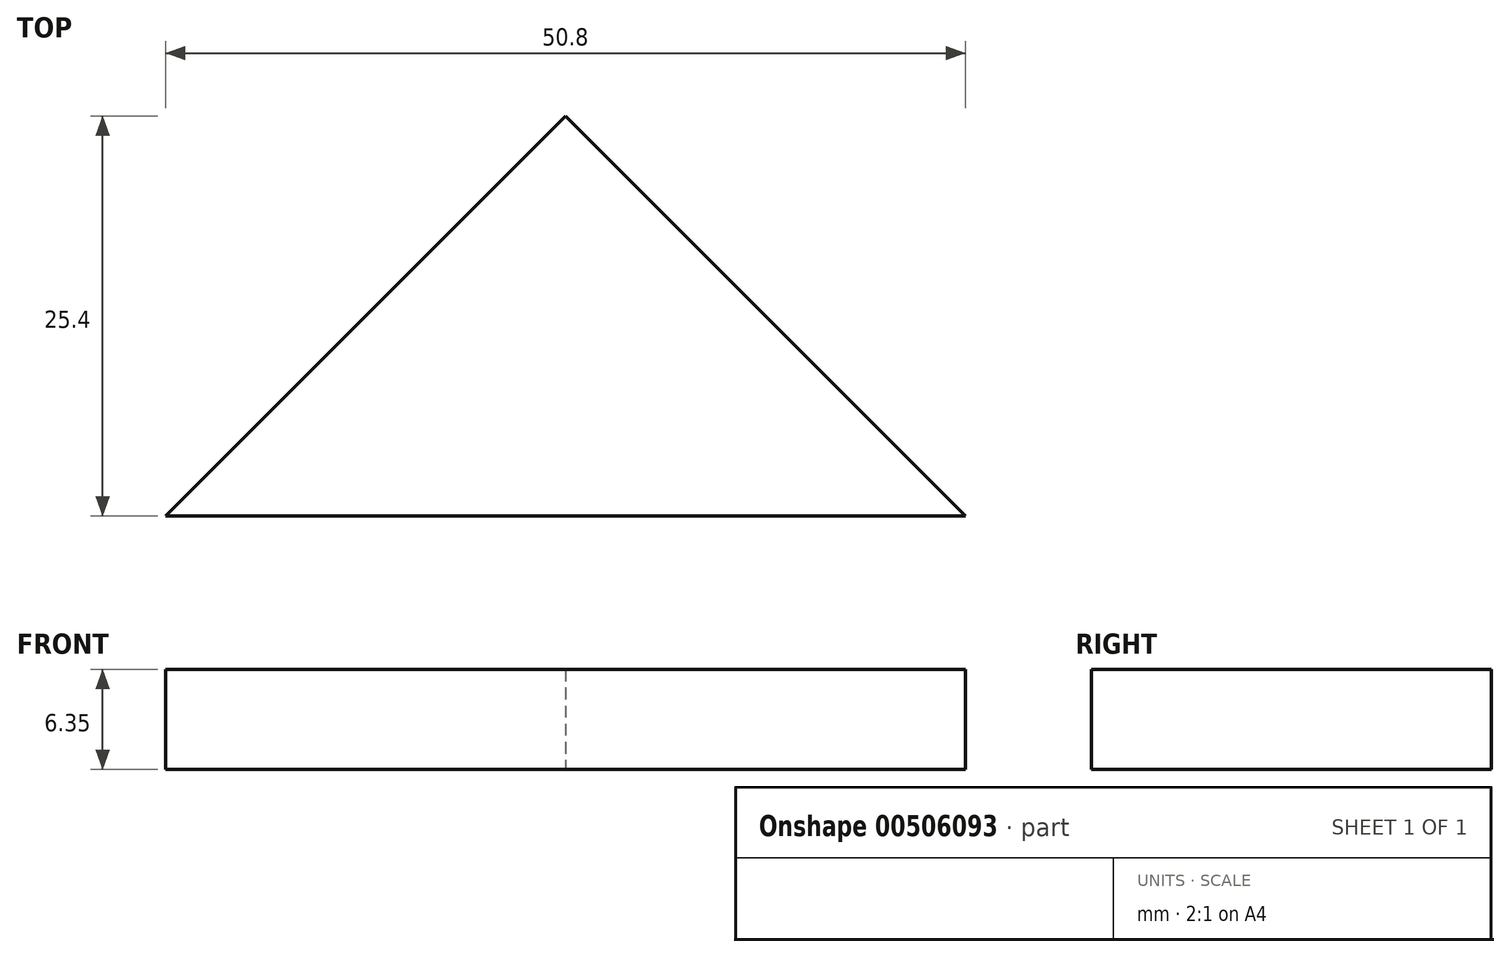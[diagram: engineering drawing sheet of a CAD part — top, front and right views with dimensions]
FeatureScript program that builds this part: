
annotation { "Feature Type Name" : "Feature", "Feature Type Description" : "" }
export const myFeature = defineFeature(function(context is Context, id is Id, definition is map)
    precondition{}
    {
        {
            var Q0;
            Q0=qCreatedBy(makeId("Top.planeOp"),FACE);
            var sketch = newSketch(context, id + "F0", { "sketchPlane" : qUnion([Q0])});
            skLineSegment(sketch, "E0.bottom", {"start": v(0, 0) * mm, "end": v(50.8, 0) * mm});
            skLineSegment(sketch, "E1", {"start": v(25.4, 25.4) * mm, "end": v(50.8, 0) * mm});
            skLineSegment(sketch, "E2", {"start": v(0, 0) * mm, "end": v(25.4, 25.4) * mm});
            skSolve(sketch);
        }
        {
            var Q0;
            Q0=makeQuery(id+"F0.imprint","IMPRINT",FACE,{"disambiguationData":[TD([[makeQuery(id+"F0.imprint","IMPRINT",EDGE,{"derivedFrom":sQuery(id+"F0.wireOp",EDGE,"E0.bottom")}),1.0]])]});
            extrude(context, id + "F1", {"entities" : qUnion([Q0]), "depth" : 6.35 * mm});
        }
    });
